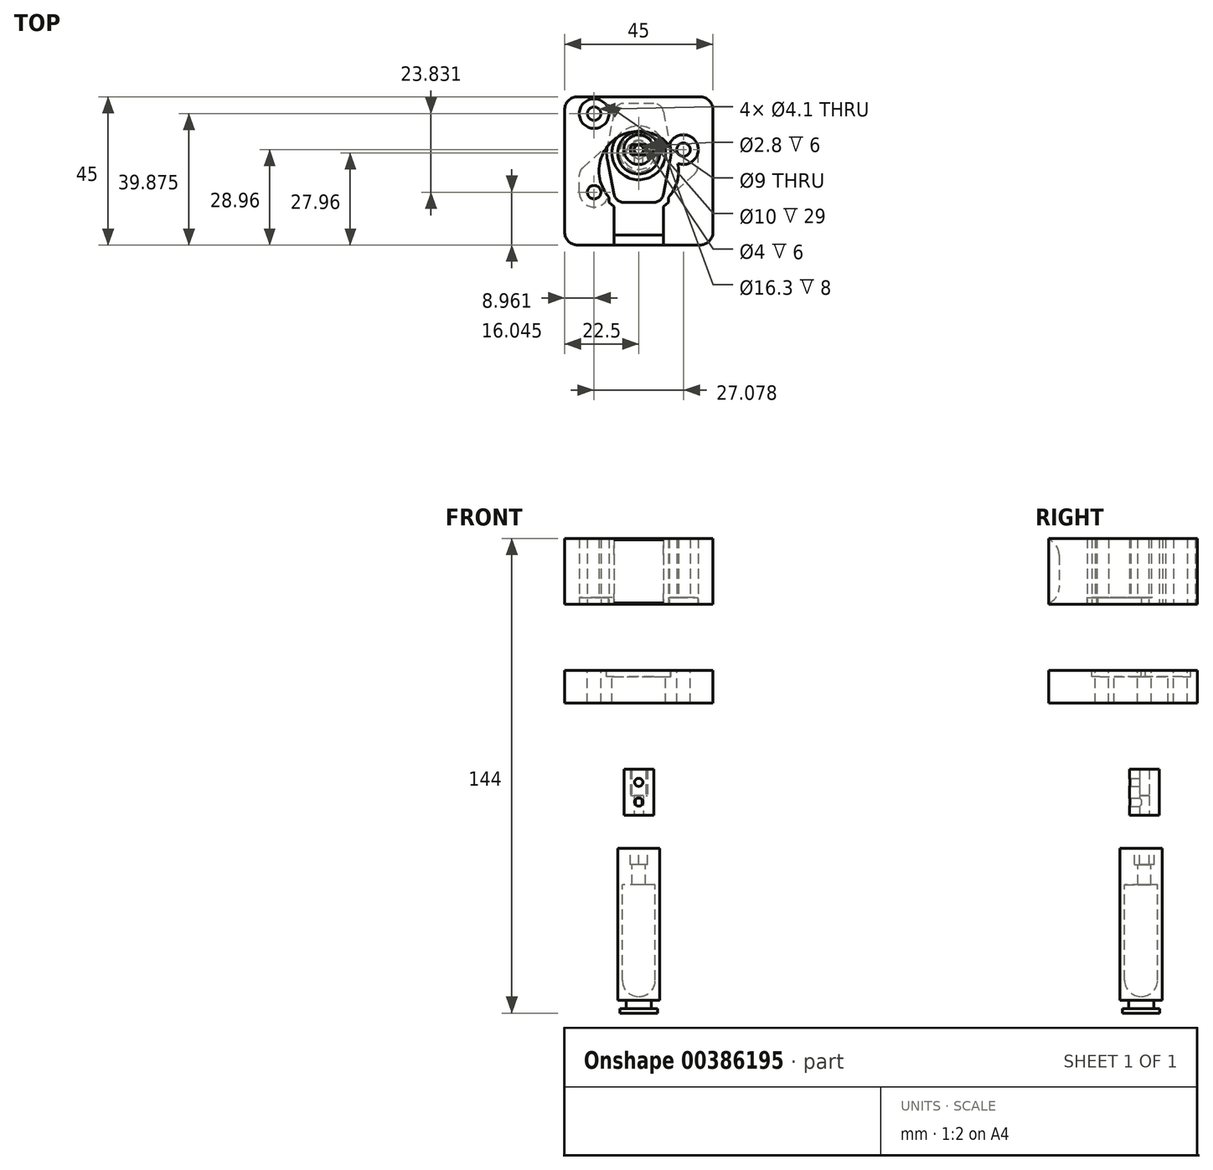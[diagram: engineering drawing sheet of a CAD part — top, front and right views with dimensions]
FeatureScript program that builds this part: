
annotation { "Feature Type Name" : "Feature", "Feature Type Description" : "" }
export const myFeature = defineFeature(function(context is Context, id is Id, definition is map)
    precondition{}
    {
        {
            assignVariable(context, id + "F0", {"name" : "plunger_h", "anyValue" : 50});
        }
        {
            assignVariable(context, id + "F1", {"name" : "M4_rivet_len", "anyValue" : 11});
        }
        {
            var Q0;
            Q0=qCreatedBy(makeId("Front.planeOp"),FACE);
            var sketch = newSketch(context, id + "F2", { "sketchPlane" : qUnion([Q0])});
            skLineSegment(sketch, "E0", {"start": v(0, 15.38) * mm, "end": v(0, -12.78) * mm, "construction": true});
            skLineSegment(sketch, "E1", {"start": v(0, 0) * mm, "end": v(5.7, 0) * mm});
            skLineSegment(sketch, "E2", {"start": v(5.7, 0) * mm, "end": v(5.7, 1.4) * mm});
            skLineSegment(sketch, "E3", {"start": v(5.7, 1.4) * mm, "end": v(3.8, 1.4) * mm});
            skLineSegment(sketch, "E4", {"start": v(3.8, 1.4) * mm, "end": v(3.8, 3.9) * mm});
            skLineSegment(sketch, "E5", {"start": v(3.8, 3.9) * mm, "end": v(6.4, 3.9) * mm});
            skLineSegment(sketch, "E6", {"start": v(6.4, 3.9) * mm, "end": v(6.4, 50) * mm});
            skLineSegment(sketch, "E7", {"start": v(6.4, 50) * mm, "end": v(5, 50) * mm});
            skLineSegment(sketch, "E8", {"start": v(5, 50) * mm, "end": v(5, 10) * mm});
            skLineSegment(sketch, "E9", {"start": v(0, 5) * mm, "end": v(0, 5) * mm});
            skLineSegment(sketch, "E10", {"start": v(0, 5) * mm, "end": v(0, 0) * mm});
            skPoint(sketch, "E11.visualSharp", {"position": v(5, 5) * mm});
            skArc(sketch, "E11.filletArc", {"start": v(0, 5) * mm, "mid": v(3.54, 6.46) * mm, "end": v(5, 10) * mm});
            skSolve(sketch);
        }
        {
            var Q0;
            Q0=makeQuery(id+"F2.imprint","IMPRINT",FACE,{"disambiguationData":[TD([[makeQuery(id+"F2.imprint","IMPRINT",EDGE,{"derivedFrom":sQuery(id+"F2.wireOp",EDGE,"E1")}),1.0]])]});
            var Q1;
            Q1=sQuery(id+"F2.wireOp",EDGE,"E0");
            revolve(context, id + "F3", {"entities" : qUnion([Q0]), "axis" : qUnion([Q1]), "revolveType" : RevolveType.FULL});
        }
        {
            var Q0;
            Q0=makeQuery(id+"F3.opRevolve","SWEPT_FACE",FACE,{"disambiguationData":[OSD([sQuery(id+"F2.wireOp",EDGE,"E7")])]});
            var sketch = newSketch(context, id + "F4", { "sketchPlane" : qUnion([Q0])});
            skCircle(sketch, "E12", {"center": v(0, 0) * mm, "radius": 5 * mm});
            skLineSegment(sketch, "E13", {"start": v(0, 11.62) * mm, "end": v(0, -12.28) * mm, "construction": true});
            skLineSegment(sketch, "E14", {"start": v(11.89, 0) * mm, "end": v(-13.02, 0) * mm, "construction": true});
            skCircle(sketch, "E15", {"center": v(0, 1) * mm, "radius": 2 * mm});
            skCircle(sketch, "E16", {"center": v(0, 1) * mm, "radius": 3 * mm});
            skCircle(sketch, "E17.cCircle", {"center": v(0, 1) * mm, "radius": 3 * mm, "construction": true});
            skLineSegment(sketch, "E17.0", {"start": v(0, -2) * mm, "end": v(-2.6, -0.5) * mm});
            skLineSegment(sketch, "E17.1", {"start": v(-2.6, -0.5) * mm, "end": v(-2.6, 2.5) * mm});
            skLineSegment(sketch, "E17.2", {"start": v(-2.6, 2.5) * mm, "end": v(0, 4) * mm});
            skLineSegment(sketch, "E17.3", {"start": v(0, 4) * mm, "end": v(2.6, 2.5) * mm});
            skLineSegment(sketch, "E17.4", {"start": v(2.6, 2.5) * mm, "end": v(2.6, -0.5) * mm});
            skLineSegment(sketch, "E17.5", {"start": v(2.6, -0.5) * mm, "end": v(0, -2) * mm});
            skSolve(sketch);
        }
        {
            var Q0;
            Q0=makeQuery(id+"F4.imprint","IMPRINT",FACE,{"disambiguationData":[TD([[makeQuery(id+"F4.imprint","IMPRINT",EDGE,{"derivedFrom":sQuery(id+"F4.wireOp",EDGE,"E12")}),1.0]])]});
            var Q1;
            Q1=makeQuery(id+"F4.imprint","IMPRINT",FACE,{"disambiguationData":[TD([[makeQuery(id+"F4.imprint","IMPRINT",EDGE,{"derivedFrom":sQuery(id+"F4.wireOp",EDGE,"E15")}),-1.0]])]});
            var Q2;
            {var subQ0=sQuery(id+"F4.wireOp",EDGE,"E17.0");Q2=makeQuery(id+"F4.imprint","IMPRINT",FACE,{"disambiguationData":[TD([[makeQuery(id+"F4.imprint","IMPRINT",EDGE,{"derivedFrom":subQ0}),1.0]])]});}
            var Q3;
            {var subQ0=sQuery(id+"F4.wireOp",EDGE,"E17.1");Q3=makeQuery(id+"F4.imprint","IMPRINT",FACE,{"disambiguationData":[TD([[makeQuery(id+"F4.imprint","IMPRINT",EDGE,{"derivedFrom":subQ0}),1.0]])]});}
            var Q4;
            {var subQ0=sQuery(id+"F4.wireOp",EDGE,"E17.2");Q4=makeQuery(id+"F4.imprint","IMPRINT",FACE,{"disambiguationData":[TD([[makeQuery(id+"F4.imprint","IMPRINT",EDGE,{"derivedFrom":subQ0}),1.0]])]});}
            var Q5;
            {var subQ0=sQuery(id+"F4.wireOp",EDGE,"E17.3");Q5=makeQuery(id+"F4.imprint","IMPRINT",FACE,{"disambiguationData":[TD([[makeQuery(id+"F4.imprint","IMPRINT",EDGE,{"derivedFrom":subQ0}),1.0]])]});}
            var Q6;
            {var subQ0=sQuery(id+"F4.wireOp",EDGE,"E17.4");Q6=makeQuery(id+"F4.imprint","IMPRINT",FACE,{"disambiguationData":[TD([[makeQuery(id+"F4.imprint","IMPRINT",EDGE,{"derivedFrom":subQ0}),1.0]])]});}
            var Q7;
            {var subQ0=sQuery(id+"F4.wireOp",EDGE,"E17.5");Q7=makeQuery(id+"F4.imprint","IMPRINT",FACE,{"disambiguationData":[TD([[makeQuery(id+"F4.imprint","IMPRINT",EDGE,{"derivedFrom":subQ0}),1.0]])]});}
            extrude(context, id + "F5", {"entities" : qUnion([Q0, Q1, Q2, Q3, Q4, Q5, Q6, Q7]), "operationType" : NewBodyOperationType.ADD, "oppositeDirection" : true, "depth" : (getVariable(context, 'M4_rivet_len')) * mm, "offsetDistance" : 25 * mm});
        }
        {
            var Q0;
            Q0=makeQuery(id+"F4.imprint","IMPRINT",FACE,{"disambiguationData":[TD([[makeQuery(id+"F4.imprint","IMPRINT",EDGE,{"derivedFrom":sQuery(id+"F4.wireOp",EDGE,"E15")}),-1.0]])]});
            extrude(context, id + "F6", {"entities" : qUnion([Q0]), "operationType" : NewBodyOperationType.REMOVE, "oppositeDirection" : true, "depth" : 5 * mm, "offsetDistance" : 25 * mm});
        }
        {
            var Q0;
            Q0=qCreatedBy(makeId("Top.planeOp"),FACE);
            cPlane(context, id + "F7", {"entities" : qUnion([Q0]), "cplaneType" : CPlaneType.OFFSET, "offset" : (getVariable(context, 'plunger_h') + 10) * mm, "width" : 150 * mm, "height" : 150 * mm});
        }
        {
            var Q0;
            Q0=qCreatedBy(id+"F7.planeOp",FACE);
            var sketch = newSketch(context, id + "F8", { "sketchPlane" : qUnion([Q0])});
            skCircle(sketch, "E18", {"center": v(0, 1) * mm, "radius": 4.5 * mm});
            skCircle(sketch, "E19", {"center": v(0, 1) * mm, "radius": 2.6 * mm});
            skLineSegment(sketch, "E20", {"start": v(-2.12, 2.5) * mm, "end": v(2.12, 2.5) * mm});
            skLineSegment(sketch, "E21", {"start": v(-2.12, -0.5) * mm, "end": v(2.12, -0.5) * mm});
            skCircle(sketch, "E22", {"center": v(0, 1) * mm, "radius": 1.4 * mm});
            skSolve(sketch);
        }
        {
            var Q0;
            Q0=makeQuery(id+"F8.imprint","IMPRINT",FACE,{"disambiguationData":[TD([[makeQuery(id+"F8.imprint","IMPRINT",EDGE,{"derivedFrom":sQuery(id+"F8.wireOp",EDGE,"E18")}),1.0]])]});
            var Q1;
            {var subQ0=sQuery(id+"F8.wireOp",EDGE,"E21");var subQ1=sQuery(id+"F8.wireOp",EDGE,"E19");var subQ2=makeQuery(id+"F8.imprint","INTERSECT",VERTEX,{"disambiguationData":[OD(0.0)],"derivedFrom":[subQ1,subQ0]});Q1=makeQuery(id+"F8.imprint","IMPRINT",FACE,{"disambiguationData":[TD([[makeQuery(id+"F8.imprint","IMPRINT",EDGE,{"disambiguationData":[TD([[subQ2,-1.0]])],"derivedFrom":subQ1}),1.0]])]});}
            var Q2;
            {var subQ0=sQuery(id+"F8.wireOp",EDGE,"E22");var subQ1=sQuery(id+"F8.wireOp",EDGE,"E20");var subQ2=makeQuery(id+"F8.imprint","INTERSECT",VERTEX,{"disambiguationData":[OD(0.0)],"derivedFrom":[subQ1,subQ0]});Q2=makeQuery(id+"F8.imprint","IMPRINT",FACE,{"disambiguationData":[TD([[makeQuery(id+"F8.imprint","IMPRINT",EDGE,{"disambiguationData":[TD([[subQ2,-1.0]])],"derivedFrom":subQ1}),1.0]])]});}
            var Q3;
            {var subQ0=sQuery(id+"F8.wireOp",EDGE,"E22");var subQ1=sQuery(id+"F8.wireOp",EDGE,"E21");var subQ2=makeQuery(id+"F8.imprint","INTERSECT",VERTEX,{"disambiguationData":[OD(0.0)],"derivedFrom":[subQ1,subQ0]});Q3=makeQuery(id+"F8.imprint","IMPRINT",FACE,{"disambiguationData":[TD([[makeQuery(id+"F8.imprint","IMPRINT",EDGE,{"disambiguationData":[TD([[subQ2,-1.0]])],"derivedFrom":subQ1}),-1.0]])]});}
            var Q4;
            {var subQ0=sQuery(id+"F8.wireOp",EDGE,"E20");var subQ1=sQuery(id+"F8.wireOp",EDGE,"E19");var subQ2=makeQuery(id+"F8.imprint","INTERSECT",VERTEX,{"disambiguationData":[OD(0.0)],"derivedFrom":[subQ1,subQ0]});Q4=makeQuery(id+"F8.imprint","IMPRINT",FACE,{"disambiguationData":[TD([[makeQuery(id+"F8.imprint","IMPRINT",EDGE,{"disambiguationData":[TD([[subQ2,1.0]])],"derivedFrom":subQ1}),1.0]])]});}
            extrude(context, id + "F9", {"entities" : qUnion([Q0, Q1, Q2, Q3, Q4]), "depth" : 14 * mm});
        }
        {
            var Q0;
            {var subQ0=sQuery(id+"F8.wireOp",EDGE,"E20");var subQ1=sQuery(id+"F8.wireOp",EDGE,"E19");var subQ2=makeQuery(id+"F8.imprint","INTERSECT",VERTEX,{"disambiguationData":[OD(0.0)],"derivedFrom":[subQ1,subQ0]});Q0=makeQuery(id+"F8.imprint","IMPRINT",FACE,{"disambiguationData":[TD([[makeQuery(id+"F8.imprint","IMPRINT",EDGE,{"disambiguationData":[TD([[subQ2,-1.0]])],"derivedFrom":subQ1}),1.0]])]});}
            var Q1;
            {var subQ0=sQuery(id+"F8.wireOp",EDGE,"E20");var subQ1=sQuery(id+"F8.wireOp",EDGE,"E19");var subQ2=makeQuery(id+"F8.imprint","INTERSECT",VERTEX,{"disambiguationData":[OD(1.0)],"derivedFrom":[subQ1,subQ0]});Q1=makeQuery(id+"F8.imprint","IMPRINT",FACE,{"disambiguationData":[TD([[makeQuery(id+"F8.imprint","IMPRINT",EDGE,{"disambiguationData":[TD([[subQ2,1.0]])],"derivedFrom":subQ1}),1.0]])]});}
            extrude(context, id + "F10", {"entities" : qUnion([Q0, Q1]), "operationType" : NewBodyOperationType.ADD, "depth" : 6 * mm});
        }
        {
            var Q0;
            Q0=qCreatedBy(makeId("Front.planeOp"),FACE);
            var sketch = newSketch(context, id + "F11", { "sketchPlane" : qUnion([Q0])});
            skCircle(sketch, "E23", {"center": v(0, 64) * mm, "radius": 1.25 * mm});
            skCircle(sketch, "E24", {"center": v(0, 70) * mm, "radius": 1.25 * mm});
            skSolve(sketch);
        }
        {
            var Q0;
            Q0=makeQuery(id+"F11.imprint","IMPRINT",FACE,{"disambiguationData":[TD([[makeQuery(id+"F11.imprint","IMPRINT",EDGE,{"derivedFrom":sQuery(id+"F11.wireOp",EDGE,"E24")}),1.0]])]});
            var Q1;
            Q1=makeQuery(id+"F11.imprint","IMPRINT",FACE,{"disambiguationData":[TD([[makeQuery(id+"F11.imprint","IMPRINT",EDGE,{"derivedFrom":sQuery(id+"F11.wireOp",EDGE,"E23")}),1.0]])]});
            var Q2;
            Q2=sQuery(id+"F11.wireOp",EDGE,"E24");
            var Q3;
            Q3=sQuery(id+"F11.wireOp",EDGE,"E23");
            extrude(context, id + "F12", {"entities" : qUnion([Q0, Q1]), "operationType" : NewBodyOperationType.REMOVE, "surfaceEntities" : qUnion([Q2, Q3]), "endBound" : BoundingType.THROUGH_ALL, "depth" : 25 * mm});
        }
        {
            var Q0;
            Q0=makeQuery(id+"F9.opExtrude","CAP_FACE",FACE,{"disambiguationData":[OSD([sQuery(id+"F8.wireOp",EDGE,"E18"),sQuery(id+"F8.wireOp",EDGE,"E19"),sQuery(id+"F8.wireOp",EDGE,"E20"),sQuery(id+"F8.wireOp",EDGE,"E21")])],"isStart":false});
            cPlane(context, id + "F13", {"entities" : qUnion([Q0]), "cplaneType" : CPlaneType.OFFSET, "offset" : 50 * mm, "width" : 150 * mm, "height" : 150 * mm});
        }
        {
            var Q0;
            Q0=qCreatedBy(id+"F13.planeOp",FACE);
            var sketch = newSketch(context, id + "F14", { "sketchPlane" : qUnion([Q0])});
            skLineSegment(sketch, "E25", {"start": v(0, -36.46) * mm, "end": v(0, 8.54) * mm, "construction": true});
            skArc(sketch, "E26", {"start": v(7.5, -14.89) * mm, "mid": v(0, 6.6) * mm, "end": v(-7.5, -14.89) * mm});
            skLineSegment(sketch, "E27.top", {"start": v(-7.5, -24.89) * mm, "end": v(7.5, -24.89) * mm});
            skLineSegment(sketch, "E27.left", {"start": v(-7.5, -14.89) * mm, "end": v(-7.5, -24.89) * mm});
            skLineSegment(sketch, "E27.right", {"start": v(7.5, -14.89) * mm, "end": v(7.5, -24.89) * mm});
            skLineSegment(sketch, "E28", {"start": v(-28.87, -5.46) * mm, "end": v(25.7, -5.46) * mm, "construction": true});
            skCircle(sketch, "E29", {"center": v(-13.54, -11.92) * mm, "radius": 2.05 * mm});
            skLineSegment(sketch, "E30", {"start": v(21.88, 4.98) * mm, "end": v(-18.35, -14.21) * mm, "construction": true});
            skLineSegment(sketch, "E31", {"start": v(-2.48, -0.26) * mm, "end": v(2.36, -10.4) * mm, "construction": true});
            skCircle(sketch, "E32.MirrorC", {"center": v(13.54, 1) * mm, "radius": 2.05 * mm});
            skCircle(sketch, "E33", {"center": v(-13.54, -11.92) * mm, "radius": 4.5 * mm});
            skCircle(sketch, "E34.MirrorC", {"center": v(13.54, 1) * mm, "radius": 4.5 * mm});
            skLineSegment(sketch, "E35", {"start": v(-13.54, 1) * mm, "end": v(16.76, 1) * mm, "construction": true});
            skLineSegment(sketch, "E36.bottom", {"start": v(-18.5, -27.96) * mm, "end": v(18.5, -27.96) * mm});
            skLineSegment(sketch, "E36.top", {"start": v(-18.5, 17.04) * mm, "end": v(18.5, 17.04) * mm});
            skLineSegment(sketch, "E36.left", {"start": v(-22.5, -23.96) * mm, "end": v(-22.5, 13.04) * mm});
            skLineSegment(sketch, "E36.right", {"start": v(22.5, -23.96) * mm, "end": v(22.5, 13.04) * mm});
            skLineSegment(sketch, "E37", {"start": v(17.93, 0) * mm, "end": v(17.93, -5.46) * mm});
            skLineSegment(sketch, "E38", {"start": v(17.93, -5.46) * mm, "end": v(8.1, -14.38) * mm});
            skLineSegment(sketch, "E39", {"start": v(-18.04, -11.92) * mm, "end": v(-18.04, -5.46) * mm});
            skLineSegment(sketch, "E40", {"start": v(-18.04, -5.46) * mm, "end": v(-8.05, 3.5) * mm});
            skLineSegment(sketch, "E41", {"start": v(7.5, -16.33) * mm, "end": v(9, -14.97) * mm});
            skLineSegment(sketch, "E42", {"start": v(9, -14.97) * mm, "end": v(9, -13.47) * mm});
            skLineSegment(sketch, "E43.MirrorCS", {"start": v(-9, -14.97) * mm, "end": v(-9, -13.47) * mm});
            skLineSegment(sketch, "E44.MirrorCS", {"start": v(-7.5, -16.33) * mm, "end": v(-9, -14.97) * mm});
            skCircle(sketch, "E45.MirrorC", {"center": v(-13.54, 11.92) * mm, "radius": 4.5 * mm});
            skCircle(sketch, "E46.MirrorC", {"center": v(-13.54, 11.92) * mm, "radius": 2.05 * mm});
            skPoint(sketch, "E47.visualSharp", {"position": v(-22.5, 17.04) * mm});
            skArc(sketch, "E47.filletArc", {"start": v(-18.5, 17.04) * mm, "mid": v(-21.33, 15.87) * mm, "end": v(-22.5, 13.04) * mm});
            skPoint(sketch, "E48.visualSharp", {"position": v(22.5, 17.04) * mm});
            skArc(sketch, "E48.filletArc", {"start": v(22.5, 13.04) * mm, "mid": v(21.33, 15.87) * mm, "end": v(18.5, 17.04) * mm});
            skPoint(sketch, "E49.visualSharp", {"position": v(-22.5, -27.96) * mm});
            skArc(sketch, "E49.filletArc", {"start": v(-22.5, -23.96) * mm, "mid": v(-21.33, -26.79) * mm, "end": v(-18.5, -27.96) * mm});
            skPoint(sketch, "E50.visualSharp", {"position": v(22.5, -27.96) * mm});
            skArc(sketch, "E50.filletArc", {"start": v(18.5, -27.96) * mm, "mid": v(21.33, -26.79) * mm, "end": v(22.5, -23.96) * mm});
            skLineSegment(sketch, "E51", {"start": v(-18.5, 17.04) * mm, "end": v(-18.5, -27.96) * mm});
            skLineSegment(sketch, "E52", {"start": v(18.5, 17.04) * mm, "end": v(18.5, -27.96) * mm});
            skSolve(sketch);
        }
        {
            var Q0;
            Q0=makeQuery(id+"F14.imprint","IMPRINT",FACE,{"disambiguationData":[TD([[makeQuery(id+"F14.imprint","IMPRINT",EDGE,{"derivedFrom":sQuery(id+"F14.wireOp",EDGE,"E36.right")}),1.0]])]});
            var Q1;
            {var subQ6=sQuery(id+"F14.wireOp",EDGE,"E27.top");Q1=makeQuery(id+"F14.imprint","IMPRINT",FACE,{"disambiguationData":[TD([[makeQuery(id+"F14.imprint","IMPRINT",EDGE,{"derivedFrom":subQ6}),-1.0]])]});}
            var Q2;
            {var subQ5=sQuery(id+"F14.wireOp",EDGE,"E36.top");Q2=makeQuery(id+"F14.imprint","IMPRINT",FACE,{"disambiguationData":[TD([[makeQuery(id+"F14.imprint","IMPRINT",EDGE,{"derivedFrom":subQ5}),-1.0]])]});}
            var Q3;
            Q3=makeQuery(id+"F14.imprint","IMPRINT",FACE,{"disambiguationData":[TD([[makeQuery(id+"F14.imprint","IMPRINT",EDGE,{"derivedFrom":sQuery(id+"F14.wireOp",EDGE,"E36.left")}),-1.0]])]});
            var Q4;
            Q4=makeQuery(id+"F14.imprint","IMPRINT",FACE,{"disambiguationData":[TD([[makeQuery(id+"F14.imprint","IMPRINT",EDGE,{"derivedFrom":sQuery(id+"F14.wireOp",EDGE,"E46.MirrorC")}),1.0]])]});
            var Q5;
            Q5=makeQuery(id+"F14.imprint","IMPRINT",FACE,{"disambiguationData":[TD([[makeQuery(id+"F14.imprint","IMPRINT",EDGE,{"derivedFrom":sQuery(id+"F14.wireOp",EDGE,"E29")}),-1.0]])]});
            var Q6;
            {var subQ0=sQuery(id+"F14.wireOp",EDGE,"E40");var subQ1=sQuery(id+"F14.wireOp",EDGE,"E26");var subQ2=makeQuery(id+"F14.imprint","INTERSECT",VERTEX,{"derivedFrom":[subQ1,subQ0]});Q6=makeQuery(id+"F14.imprint","IMPRINT",FACE,{"disambiguationData":[TD([[makeQuery(id+"F14.imprint","IMPRINT",EDGE,{"disambiguationData":[TD([[subQ2,-1.0]])],"derivedFrom":subQ1}),-1.0]])]});}
            var Q7;
            {var subQ0=sQuery(id+"F14.wireOp",EDGE,"E42");var subQ1=sQuery(id+"F14.wireOp",EDGE,"E26");var subQ2=makeQuery(id+"F14.imprint","INTERSECT",VERTEX,{"derivedFrom":[subQ1,subQ0]});Q7=makeQuery(id+"F14.imprint","IMPRINT",FACE,{"disambiguationData":[TD([[makeQuery(id+"F14.imprint","IMPRINT",EDGE,{"disambiguationData":[TD([[subQ2,-1.0]])],"derivedFrom":subQ1}),-1.0]])]});}
            var Q8;
            {var subQ0=sQuery(id+"F14.wireOp",EDGE,"E37");Q8=makeQuery(id+"F14.imprint","IMPRINT",FACE,{"disambiguationData":[TD([[makeQuery(id+"F14.imprint","IMPRINT",EDGE,{"derivedFrom":subQ0}),-1.0]])]});}
            var Q9;
            Q9=makeQuery(id+"F14.imprint","IMPRINT",FACE,{"disambiguationData":[TD([[makeQuery(id+"F14.imprint","IMPRINT",EDGE,{"derivedFrom":sQuery(id+"F14.wireOp",EDGE,"E32.MirrorC")}),1.0]])]});
            var Q10;
            {var subQ0=sQuery(id+"F14.wireOp",EDGE,"E34.MirrorC");var subQ1=makeQuery(id+"F14.imprint","INTERSECT",VERTEX,{"derivedFrom":[subQ0,sQuery(id+"F14.wireOp",EDGE,"E37")]});Q10=makeQuery(id+"F14.imprint","IMPRINT",FACE,{"disambiguationData":[TD([[makeQuery(id+"F14.imprint","IMPRINT",EDGE,{"disambiguationData":[TD([[subQ1,1.0]])],"derivedFrom":subQ0}),-1.0]])]});}
            var Q11;
            {var subQ0=sQuery(id+"F14.wireOp",EDGE,"E39");Q11=makeQuery(id+"F14.imprint","IMPRINT",FACE,{"disambiguationData":[TD([[makeQuery(id+"F14.imprint","IMPRINT",EDGE,{"derivedFrom":subQ0}),-1.0]])]});}
            var Q12;
            {var subQ0=sQuery(id+"F14.wireOp",EDGE,"E51");var subQ1=sQuery(id+"F14.wireOp",EDGE,"E45.MirrorC");var subQ2=makeQuery(id+"F14.imprint","INTERSECT",VERTEX,{"disambiguationData":[OD(0.0)],"derivedFrom":[subQ1,subQ0]});Q12=makeQuery(id+"F14.imprint","IMPRINT",FACE,{"disambiguationData":[TD([[makeQuery(id+"F14.imprint","IMPRINT",EDGE,{"disambiguationData":[TD([[subQ2,1.0]])],"derivedFrom":subQ1}),-1.0]])]});}
            var Q13;
            {var subQ0=sQuery(id+"F14.wireOp",EDGE,"E33");var subQ1=makeQuery(id+"F14.imprint","INTERSECT",VERTEX,{"derivedFrom":[subQ0,sQuery(id+"F14.wireOp",EDGE,"E39")]});Q13=makeQuery(id+"F14.imprint","IMPRINT",FACE,{"disambiguationData":[TD([[makeQuery(id+"F14.imprint","IMPRINT",EDGE,{"disambiguationData":[TD([[subQ1,-1.0]])],"derivedFrom":subQ0}),1.0]])]});}
            extrude(context, id + "F15", {"entities" : qUnion([Q0, Q1, Q2, Q3, Q4, Q5, Q6, Q7, Q8, Q9, Q10, Q11, Q12, Q13]), "depth" : 20 * mm});
        }
        {
            var Q0;
            {var subQ0=sQuery(id+"F14.wireOp",EDGE,"E42");var subQ1=sQuery(id+"F14.wireOp",EDGE,"E26");var subQ2=makeQuery(id+"F14.imprint","INTERSECT",VERTEX,{"derivedFrom":[subQ1,subQ0]});Q0=makeQuery(id+"F14.imprint","IMPRINT",FACE,{"disambiguationData":[TD([[makeQuery(id+"F14.imprint","IMPRINT",EDGE,{"disambiguationData":[TD([[subQ2,-1.0]])],"derivedFrom":subQ1}),-1.0]])]});}
            var Q1;
            Q1=makeQuery(id+"F14.imprint","IMPRINT",FACE,{"disambiguationData":[TD([[makeQuery(id+"F14.imprint","IMPRINT",EDGE,{"derivedFrom":sQuery(id+"F14.wireOp",EDGE,"E32.MirrorC")}),1.0]])]});
            var Q2;
            Q2=makeQuery(id+"F14.imprint","IMPRINT",FACE,{"disambiguationData":[TD([[makeQuery(id+"F14.imprint","IMPRINT",EDGE,{"derivedFrom":sQuery(id+"F14.wireOp",EDGE,"E29")}),-1.0]])]});
            var Q3;
            {var subQ0=sQuery(id+"F14.wireOp",EDGE,"E40");var subQ1=sQuery(id+"F14.wireOp",EDGE,"E26");var subQ2=makeQuery(id+"F14.imprint","INTERSECT",VERTEX,{"derivedFrom":[subQ1,subQ0]});Q3=makeQuery(id+"F14.imprint","IMPRINT",FACE,{"disambiguationData":[TD([[makeQuery(id+"F14.imprint","IMPRINT",EDGE,{"disambiguationData":[TD([[subQ2,-1.0]])],"derivedFrom":subQ1}),-1.0]])]});}
            var Q4;
            {var subQ0=sQuery(id+"F14.wireOp",EDGE,"E37");Q4=makeQuery(id+"F14.imprint","IMPRINT",FACE,{"disambiguationData":[TD([[makeQuery(id+"F14.imprint","IMPRINT",EDGE,{"derivedFrom":subQ0}),-1.0]])]});}
            var Q5;
            {var subQ0=sQuery(id+"F14.wireOp",EDGE,"E34.MirrorC");var subQ1=makeQuery(id+"F14.imprint","INTERSECT",VERTEX,{"derivedFrom":[subQ0,sQuery(id+"F14.wireOp",EDGE,"E37")]});Q5=makeQuery(id+"F14.imprint","IMPRINT",FACE,{"disambiguationData":[TD([[makeQuery(id+"F14.imprint","IMPRINT",EDGE,{"disambiguationData":[TD([[subQ1,1.0]])],"derivedFrom":subQ0}),-1.0]])]});}
            var Q6;
            {var subQ0=sQuery(id+"F14.wireOp",EDGE,"E39");Q6=makeQuery(id+"F14.imprint","IMPRINT",FACE,{"disambiguationData":[TD([[makeQuery(id+"F14.imprint","IMPRINT",EDGE,{"derivedFrom":subQ0}),-1.0]])]});}
            var Q7;
            {var subQ0=sQuery(id+"F14.wireOp",EDGE,"E33");var subQ1=makeQuery(id+"F14.imprint","INTERSECT",VERTEX,{"derivedFrom":[subQ0,sQuery(id+"F14.wireOp",EDGE,"E39")]});Q7=makeQuery(id+"F14.imprint","IMPRINT",FACE,{"disambiguationData":[TD([[makeQuery(id+"F14.imprint","IMPRINT",EDGE,{"disambiguationData":[TD([[subQ1,-1.0]])],"derivedFrom":subQ0}),1.0]])]});}
            extrude(context, id + "F16", {"entities" : qUnion([Q0, Q1, Q2, Q3, Q4, Q5, Q6, Q7]), "operationType" : NewBodyOperationType.REMOVE, "depth" : 2 * mm});
        }
        {
            var Q0;
            Q0=makeQuery(id+"F15.opExtrude","CAP_FACE",FACE,{"disambiguationData":[OSD([sQuery(id+"F14.wireOp",EDGE,"E26"),sQuery(id+"F14.wireOp",EDGE,"E27.top"),sQuery(id+"F14.wireOp",EDGE,"E27.left"),sQuery(id+"F14.wireOp",EDGE,"E27.right"),sQuery(id+"F14.wireOp",EDGE,"E29"),sQuery(id+"F14.wireOp",EDGE,"E32.MirrorC"),sQuery(id+"F14.wireOp",EDGE,"E36.bottom"),sQuery(id+"F14.wireOp",EDGE,"E36.top"),sQuery(id+"F14.wireOp",EDGE,"E36.left"),sQuery(id+"F14.wireOp",EDGE,"E36.right")])],"isStart":true});
            cPlane(context, id + "F17", {"entities" : qUnion([Q0]), "cplaneType" : CPlaneType.OFFSET, "offset" : 20 * mm, "width" : 150 * mm, "height" : 150 * mm});
        }
        {
            var Q0;
            Q0=qCreatedBy(id+"F17.planeOp",FACE);
            var sketch = newSketch(context, id + "F18", { "sketchPlane" : qUnion([Q0])});
            skLineSegment(sketch, "E53.bottom", {"start": v(-18.5, -17.04) * mm, "end": v(18.5, -17.04) * mm});
            skLineSegment(sketch, "E53.top", {"start": v(-18.5, 27.96) * mm, "end": v(18.5, 27.96) * mm});
            skLineSegment(sketch, "E53.left", {"start": v(-22.5, -13.04) * mm, "end": v(-22.5, 23.96) * mm});
            skLineSegment(sketch, "E53.right", {"start": v(22.5, -13.04) * mm, "end": v(22.5, 23.96) * mm});
            skCircle(sketch, "E54", {"center": v(0, 0) * mm, "radius": 8.15 * mm});
            skCircle(sketch, "E55", {"center": v(-13.54, 11.92) * mm, "radius": 2.05 * mm});
            skCircle(sketch, "E56", {"center": v(13.54, -1) * mm, "radius": 2.05 * mm});
            skCircle(sketch, "E57", {"center": v(0, 0) * mm, "radius": 9.75 * mm});
            skLineSegment(sketch, "E58", {"start": v(0, 15) * mm, "end": v(4.53, 15) * mm});
            skLineSegment(sketch, "E59", {"start": v(7.47, 12.58) * mm, "end": v(9.57, 1.87) * mm});
            skPoint(sketch, "E60.visualSharp", {"position": v(7, 15) * mm});
            skArc(sketch, "E60.filletArc", {"start": v(7.47, 12.58) * mm, "mid": v(6.44, 14.32) * mm, "end": v(4.53, 15) * mm});
            skLineSegment(sketch, "E61.MirrorCS", {"start": v(0, 15) * mm, "end": v(-4.53, 15) * mm});
            skArc(sketch, "E62.MirrorCS", {"start": v(-7.47, 12.58) * mm, "mid": v(-6.44, 14.32) * mm, "end": v(-4.53, 15) * mm});
            skLineSegment(sketch, "E63.MirrorCS", {"start": v(-7.47, 12.58) * mm, "end": v(-9.57, 1.87) * mm});
            skLineSegment(sketch, "E64.MirrorCS", {"start": v(-7.47, -12.58) * mm, "end": v(-9.57, -1.87) * mm});
            skArc(sketch, "E65.MirrorCS", {"start": v(-7.47, -12.58) * mm, "mid": v(-6.44, -14.32) * mm, "end": v(-4.53, -15) * mm});
            skLineSegment(sketch, "E66.MirrorCS", {"start": v(0, -15) * mm, "end": v(4.53, -15) * mm});
            skLineSegment(sketch, "E67.MirrorCS", {"start": v(0, -15) * mm, "end": v(-4.53, -15) * mm});
            skArc(sketch, "E68.MirrorCS", {"start": v(7.47, -12.58) * mm, "mid": v(6.44, -14.32) * mm, "end": v(4.53, -15) * mm});
            skLineSegment(sketch, "E69.MirrorCS", {"start": v(7.47, -12.58) * mm, "end": v(9.57, -1.87) * mm});
            skCircle(sketch, "E70", {"center": v(-13.54, -11.92) * mm, "radius": 2.05 * mm});
            skArc(sketch, "E71", {"start": v(-22.5, -13.04) * mm, "mid": v(-21.33, -15.87) * mm, "end": v(-18.5, -17.04) * mm});
            skArc(sketch, "E72", {"start": v(18.5, -17.04) * mm, "mid": v(21.33, -15.87) * mm, "end": v(22.5, -13.04) * mm});
            skArc(sketch, "E73", {"start": v(22.5, 23.96) * mm, "mid": v(21.33, 26.79) * mm, "end": v(18.5, 27.96) * mm});
            skArc(sketch, "E74", {"start": v(-18.5, 27.96) * mm, "mid": v(-21.33, 26.79) * mm, "end": v(-22.5, 23.96) * mm});
            skLineSegment(sketch, "E75", {"start": v(18.5, -17.04) * mm, "end": v(18.5, 27.96) * mm});
            skLineSegment(sketch, "E76", {"start": v(-18.5, -17.04) * mm, "end": v(-18.5, 27.96) * mm});
            skCircle(sketch, "E77", {"center": v(-13.54, 11.92) * mm, "radius": 3.9 * mm});
            skCircle(sketch, "E78", {"center": v(13.54, -1) * mm, "radius": 3.9 * mm});
            skCircle(sketch, "E79", {"center": v(-13.54, -11.92) * mm, "radius": 3.9 * mm});
            skLineSegment(sketch, "E80", {"start": v(-13.54, 24.89) * mm, "end": v(-13.54, -23.04) * mm, "construction": true});
            skLineSegment(sketch, "E81", {"start": v(13.54, 10.2) * mm, "end": v(13.54, -10.72) * mm, "construction": true});
            skCircle(sketch, "E82.cCircle", {"center": v(-13.54, 11.92) * mm, "radius": 3.9 * mm, "construction": true});
            skLineSegment(sketch, "E82.0", {"start": v(-13.54, 8.02) * mm, "end": v(-16.92, 9.97) * mm});
            skLineSegment(sketch, "E82.1", {"start": v(-16.92, 9.97) * mm, "end": v(-16.92, 13.87) * mm});
            skLineSegment(sketch, "E82.2", {"start": v(-16.92, 13.87) * mm, "end": v(-13.54, 15.82) * mm});
            skLineSegment(sketch, "E82.3", {"start": v(-13.54, 15.82) * mm, "end": v(-10.16, 13.87) * mm});
            skLineSegment(sketch, "E82.4", {"start": v(-10.16, 13.87) * mm, "end": v(-10.16, 9.97) * mm});
            skLineSegment(sketch, "E82.5", {"start": v(-10.16, 9.97) * mm, "end": v(-13.54, 8.02) * mm});
            skCircle(sketch, "E83.cCircle", {"center": v(-13.54, -11.92) * mm, "radius": 3.9 * mm, "construction": true});
            skLineSegment(sketch, "E83.0", {"start": v(-13.54, -15.82) * mm, "end": v(-16.92, -13.87) * mm});
            skLineSegment(sketch, "E83.1", {"start": v(-16.92, -13.87) * mm, "end": v(-16.92, -9.97) * mm});
            skLineSegment(sketch, "E83.2", {"start": v(-16.92, -9.97) * mm, "end": v(-13.54, -8.02) * mm});
            skLineSegment(sketch, "E83.3", {"start": v(-13.54, -8.02) * mm, "end": v(-10.16, -9.97) * mm});
            skLineSegment(sketch, "E83.4", {"start": v(-10.16, -9.97) * mm, "end": v(-10.16, -13.87) * mm});
            skLineSegment(sketch, "E83.5", {"start": v(-10.16, -13.87) * mm, "end": v(-13.54, -15.82) * mm});
            skCircle(sketch, "E84.cCircle", {"center": v(13.54, -1) * mm, "radius": 3.9 * mm, "construction": true});
            skLineSegment(sketch, "E84.0", {"start": v(13.54, -4.9) * mm, "end": v(10.16, -2.95) * mm});
            skLineSegment(sketch, "E84.1", {"start": v(10.16, -2.95) * mm, "end": v(10.16, 0.95) * mm});
            skLineSegment(sketch, "E84.2", {"start": v(10.16, 0.95) * mm, "end": v(13.54, 2.9) * mm});
            skLineSegment(sketch, "E84.3", {"start": v(13.54, 2.9) * mm, "end": v(16.92, 0.95) * mm});
            skLineSegment(sketch, "E84.4", {"start": v(16.92, 0.95) * mm, "end": v(16.92, -2.95) * mm});
            skLineSegment(sketch, "E84.5", {"start": v(16.92, -2.95) * mm, "end": v(13.54, -4.9) * mm});
            skSolve(sketch);
        }
        {
            var Q0;
            Q0=makeQuery(id+"F18.imprint","IMPRINT",FACE,{"disambiguationData":[TD([[makeQuery(id+"F18.imprint","IMPRINT",EDGE,{"derivedFrom":sQuery(id+"F18.wireOp",EDGE,"E53.bottom")}),1.0]])]});
            var Q1;
            {var subQ0=sQuery(id+"F18.wireOp",EDGE,"E64.MirrorCS");Q1=makeQuery(id+"F18.imprint","IMPRINT",FACE,{"disambiguationData":[TD([[makeQuery(id+"F18.imprint","IMPRINT",EDGE,{"derivedFrom":subQ0}),-1.0]])]});}
            var Q2;
            Q2=makeQuery(id+"F18.imprint","IMPRINT",FACE,{"disambiguationData":[TD([[makeQuery(id+"F18.imprint","IMPRINT",EDGE,{"derivedFrom":sQuery(id+"F18.wireOp",EDGE,"E58")}),-1.0]])]});
            var Q3;
            Q3=makeQuery(id+"F18.imprint","IMPRINT",FACE,{"disambiguationData":[TD([[makeQuery(id+"F18.imprint","IMPRINT",EDGE,{"derivedFrom":sQuery(id+"F18.wireOp",EDGE,"E54")}),-1.0]])]});
            var Q4;
            Q4=makeQuery(id+"F18.imprint","IMPRINT",FACE,{"disambiguationData":[TD([[makeQuery(id+"F18.imprint","IMPRINT",EDGE,{"derivedFrom":sQuery(id+"F18.wireOp",EDGE,"E53.left")}),-1.0]])]});
            var Q5;
            Q5=makeQuery(id+"F18.imprint","IMPRINT",FACE,{"disambiguationData":[TD([[makeQuery(id+"F18.imprint","IMPRINT",EDGE,{"derivedFrom":sQuery(id+"F18.wireOp",EDGE,"E53.right")}),1.0]])]});
            var Q6;
            {var subQ0=sQuery(id+"F18.wireOp",EDGE,"E83.2");Q6=makeQuery(id+"F18.imprint","IMPRINT",FACE,{"disambiguationData":[TD([[makeQuery(id+"F18.imprint","IMPRINT",EDGE,{"derivedFrom":subQ0}),1.0]])]});}
            var Q7;
            {var subQ0=sQuery(id+"F18.wireOp",EDGE,"E83.1");Q7=makeQuery(id+"F18.imprint","IMPRINT",FACE,{"disambiguationData":[TD([[makeQuery(id+"F18.imprint","IMPRINT",EDGE,{"derivedFrom":subQ0}),1.0]])]});}
            var Q8;
            {var subQ0=sQuery(id+"F18.wireOp",EDGE,"E83.3");Q8=makeQuery(id+"F18.imprint","IMPRINT",FACE,{"disambiguationData":[TD([[makeQuery(id+"F18.imprint","IMPRINT",EDGE,{"derivedFrom":subQ0}),1.0]])]});}
            var Q9;
            {var subQ0=sQuery(id+"F18.wireOp",EDGE,"E83.0");Q9=makeQuery(id+"F18.imprint","IMPRINT",FACE,{"disambiguationData":[TD([[makeQuery(id+"F18.imprint","IMPRINT",EDGE,{"derivedFrom":subQ0}),1.0]])]});}
            var Q10;
            Q10=makeQuery(id+"F18.imprint","IMPRINT",FACE,{"disambiguationData":[TD([[makeQuery(id+"F18.imprint","IMPRINT",EDGE,{"derivedFrom":sQuery(id+"F18.wireOp",EDGE,"E70")}),-1.0]])]});
            var Q11;
            {var subQ0=sQuery(id+"F18.wireOp",EDGE,"E83.5");Q11=makeQuery(id+"F18.imprint","IMPRINT",FACE,{"disambiguationData":[TD([[makeQuery(id+"F18.imprint","IMPRINT",EDGE,{"derivedFrom":subQ0}),1.0]])]});}
            var Q12;
            {var subQ0=sQuery(id+"F18.wireOp",EDGE,"E83.4");Q12=makeQuery(id+"F18.imprint","IMPRINT",FACE,{"disambiguationData":[TD([[makeQuery(id+"F18.imprint","IMPRINT",EDGE,{"derivedFrom":subQ0}),1.0]])]});}
            var Q13;
            {var subQ0=sQuery(id+"F18.wireOp",EDGE,"E82.2");Q13=makeQuery(id+"F18.imprint","IMPRINT",FACE,{"disambiguationData":[TD([[makeQuery(id+"F18.imprint","IMPRINT",EDGE,{"derivedFrom":subQ0}),1.0]])]});}
            var Q14;
            Q14=makeQuery(id+"F18.imprint","IMPRINT",FACE,{"disambiguationData":[TD([[makeQuery(id+"F18.imprint","IMPRINT",EDGE,{"derivedFrom":sQuery(id+"F18.wireOp",EDGE,"E55")}),-1.0]])]});
            var Q15;
            {var subQ0=sQuery(id+"F18.wireOp",EDGE,"E82.4");Q15=makeQuery(id+"F18.imprint","IMPRINT",FACE,{"disambiguationData":[TD([[makeQuery(id+"F18.imprint","IMPRINT",EDGE,{"derivedFrom":subQ0}),1.0]])]});}
            var Q16;
            {var subQ0=sQuery(id+"F18.wireOp",EDGE,"E82.3");Q16=makeQuery(id+"F18.imprint","IMPRINT",FACE,{"disambiguationData":[TD([[makeQuery(id+"F18.imprint","IMPRINT",EDGE,{"derivedFrom":subQ0}),1.0]])]});}
            var Q17;
            {var subQ0=sQuery(id+"F18.wireOp",EDGE,"E82.5");Q17=makeQuery(id+"F18.imprint","IMPRINT",FACE,{"disambiguationData":[TD([[makeQuery(id+"F18.imprint","IMPRINT",EDGE,{"derivedFrom":subQ0}),1.0]])]});}
            var Q18;
            {var subQ0=sQuery(id+"F18.wireOp",EDGE,"E82.1");Q18=makeQuery(id+"F18.imprint","IMPRINT",FACE,{"disambiguationData":[TD([[makeQuery(id+"F18.imprint","IMPRINT",EDGE,{"derivedFrom":subQ0}),1.0]])]});}
            var Q19;
            {var subQ0=sQuery(id+"F18.wireOp",EDGE,"E82.0");Q19=makeQuery(id+"F18.imprint","IMPRINT",FACE,{"disambiguationData":[TD([[makeQuery(id+"F18.imprint","IMPRINT",EDGE,{"derivedFrom":subQ0}),1.0]])]});}
            var Q20;
            {var subQ0=sQuery(id+"F18.wireOp",EDGE,"E84.2");Q20=makeQuery(id+"F18.imprint","IMPRINT",FACE,{"disambiguationData":[TD([[makeQuery(id+"F18.imprint","IMPRINT",EDGE,{"derivedFrom":subQ0}),1.0]])]});}
            var Q21;
            Q21=makeQuery(id+"F18.imprint","IMPRINT",FACE,{"disambiguationData":[TD([[makeQuery(id+"F18.imprint","IMPRINT",EDGE,{"derivedFrom":sQuery(id+"F18.wireOp",EDGE,"E56")}),-1.0]])]});
            var Q22;
            {var subQ0=sQuery(id+"F18.wireOp",EDGE,"E84.3");Q22=makeQuery(id+"F18.imprint","IMPRINT",FACE,{"disambiguationData":[TD([[makeQuery(id+"F18.imprint","IMPRINT",EDGE,{"derivedFrom":subQ0}),1.0]])]});}
            var Q23;
            {var subQ0=sQuery(id+"F18.wireOp",EDGE,"E84.4");Q23=makeQuery(id+"F18.imprint","IMPRINT",FACE,{"disambiguationData":[TD([[makeQuery(id+"F18.imprint","IMPRINT",EDGE,{"derivedFrom":subQ0}),1.0]])]});}
            var Q24;
            {var subQ4=sQuery(id+"F18.wireOp",EDGE,"E84.1");Q24=makeQuery(id+"F18.imprint","IMPRINT",FACE,{"disambiguationData":[TD([[makeQuery(id+"F18.imprint","IMPRINT",EDGE,{"derivedFrom":subQ4}),1.0]])]});}
            var Q25;
            {var subQ0=sQuery(id+"F18.wireOp",EDGE,"E84.5");Q25=makeQuery(id+"F18.imprint","IMPRINT",FACE,{"disambiguationData":[TD([[makeQuery(id+"F18.imprint","IMPRINT",EDGE,{"derivedFrom":subQ0}),1.0]])]});}
            var Q26;
            {var subQ0=sQuery(id+"F18.wireOp",EDGE,"E84.0");Q26=makeQuery(id+"F18.imprint","IMPRINT",FACE,{"disambiguationData":[TD([[makeQuery(id+"F18.imprint","IMPRINT",EDGE,{"derivedFrom":subQ0}),1.0]])]});}
            var Q27;
            {var subQ0=sQuery(id+"F18.wireOp",EDGE,"E78");var subQ1=sQuery(id+"F18.wireOp",EDGE,"E57");var subQ2=makeQuery(id+"F18.imprint","INTERSECT",VERTEX,{"disambiguationData":[OD(0.0)],"derivedFrom":[subQ1,subQ0]});Q27=makeQuery(id+"F18.imprint","IMPRINT",FACE,{"disambiguationData":[TD([[makeQuery(id+"F18.imprint","IMPRINT",EDGE,{"disambiguationData":[TD([[subQ2,-1.0]])],"derivedFrom":subQ1}),1.0]])]});}
            extrude(context, id + "F19", {"entities" : qUnion([Q0, Q1, Q2, Q3, Q4, Q5, Q6, Q7, Q8, Q9, Q10, Q11, Q12, Q13, Q14, Q15, Q16, Q17, Q18, Q19, Q20, Q21, Q22, Q23, Q24, Q25, Q26, Q27]), "depth" : 10 * mm, "offsetDistance" : 25 * mm});
        }
        {
            var Q0;
            {var subQ0=sQuery(id+"F18.wireOp",EDGE,"E64.MirrorCS");Q0=makeQuery(id+"F18.imprint","IMPRINT",FACE,{"disambiguationData":[TD([[makeQuery(id+"F18.imprint","IMPRINT",EDGE,{"derivedFrom":subQ0}),-1.0]])]});}
            var Q1;
            Q1=makeQuery(id+"F18.imprint","IMPRINT",FACE,{"disambiguationData":[TD([[makeQuery(id+"F18.imprint","IMPRINT",EDGE,{"derivedFrom":sQuery(id+"F18.wireOp",EDGE,"E58")}),-1.0]])]});
            var Q2;
            Q2=makeQuery(id+"F18.imprint","IMPRINT",FACE,{"disambiguationData":[TD([[makeQuery(id+"F18.imprint","IMPRINT",EDGE,{"derivedFrom":sQuery(id+"F18.wireOp",EDGE,"E54")}),-1.0]])]});
            extrude(context, id + "F20", {"entities" : qUnion([Q0, Q1, Q2]), "operationType" : NewBodyOperationType.REMOVE, "depth" : 2 * mm});
        }
        {
            var Q0;
            Q0=makeQuery(id+"F16.boolean.opBoolean","COPY",EDGE,{"derivedFrom":makeQuery(id+"F16.opExtrude","SWEPT_EDGE",EDGE,{"disambiguationData":[OSD([sQuery(id+"F14.wireOp",EDGE,"E37"),sQuery(id+"F14.wireOp",EDGE,"E38")])]})});
            var Q1;
            Q1=makeQuery(id+"F16.boolean.opBoolean","COPY",EDGE,{"derivedFrom":makeQuery(id+"F16.opExtrude","SWEPT_EDGE",EDGE,{"disambiguationData":[OSD([sQuery(id+"F14.wireOp",EDGE,"E39"),sQuery(id+"F14.wireOp",EDGE,"E40")])]})});
            fillet(context, id + "F21", {"entities" : qUnion([Q0, Q1]), "radius" : 3 * mm, "tangentPropagation" : true, "allowEdgeOverflow" : false});
        }
        {
            var Q0;
            Q0=makeQuery(id+"F15.opExtrude","CAP_EDGE",EDGE,{"disambiguationData":[OSD([sQuery(id+"F14.wireOp",EDGE,"E27.top")])],"isStart":false});
            fillet(context, id + "F22", {"entities" : qUnion([Q0]), "radius" : 5 * mm, "tangentPropagation" : true, "allowEdgeOverflow" : false});
        }
        {
            var Q0;
            Q0=makeQuery(id+"F15.opExtrude","CAP_EDGE",EDGE,{"disambiguationData":[OSD([sQuery(id+"F14.wireOp",EDGE,"E27.top")])],"isStart":true});
            fillet(context, id + "F23", {"entities" : qUnion([Q0]), "radius" : 5 * mm, "tangentPropagation" : true, "allowEdgeOverflow" : false});
        }
    });
